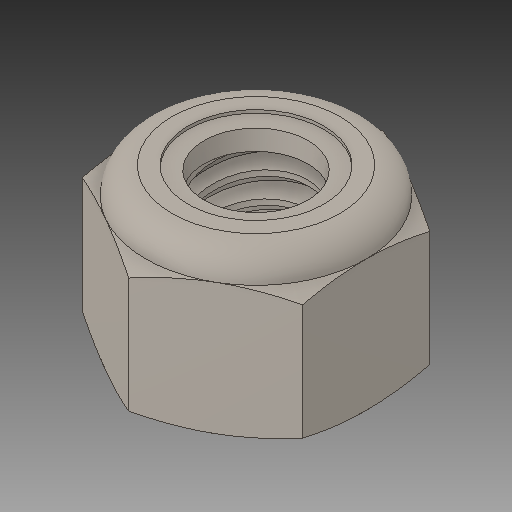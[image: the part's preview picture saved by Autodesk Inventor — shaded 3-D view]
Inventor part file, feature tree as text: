
AUTODESK INVENTOR PART (.ipt)
format: ipt  version: 2018.2 (Build 222227000, 227)  size: 303,104 bytes
history: native  units: in
note: dims shown in document units (in); Inventor stores cm internally (conversion verified against a paired STEP export)
features: other x1, revolve x1
ambient origin geometry x8: Origin, YZ Plane, XZ Plane, XY Plane, X Axis, Y Axis, Z Axis, Center Point
bodies: Solid1 (feature_tree), Solid2 (feature_tree)
feature tree (2):
  other  "Cut-Revolve4"
  revolve  "Revolve2"  [1 undecoded]
note: 1 required parameter value undecoded (feature->parameter linkage not recoverable at this tier; creation-order binding heuristic only, values carry confidence <= 0.55)
